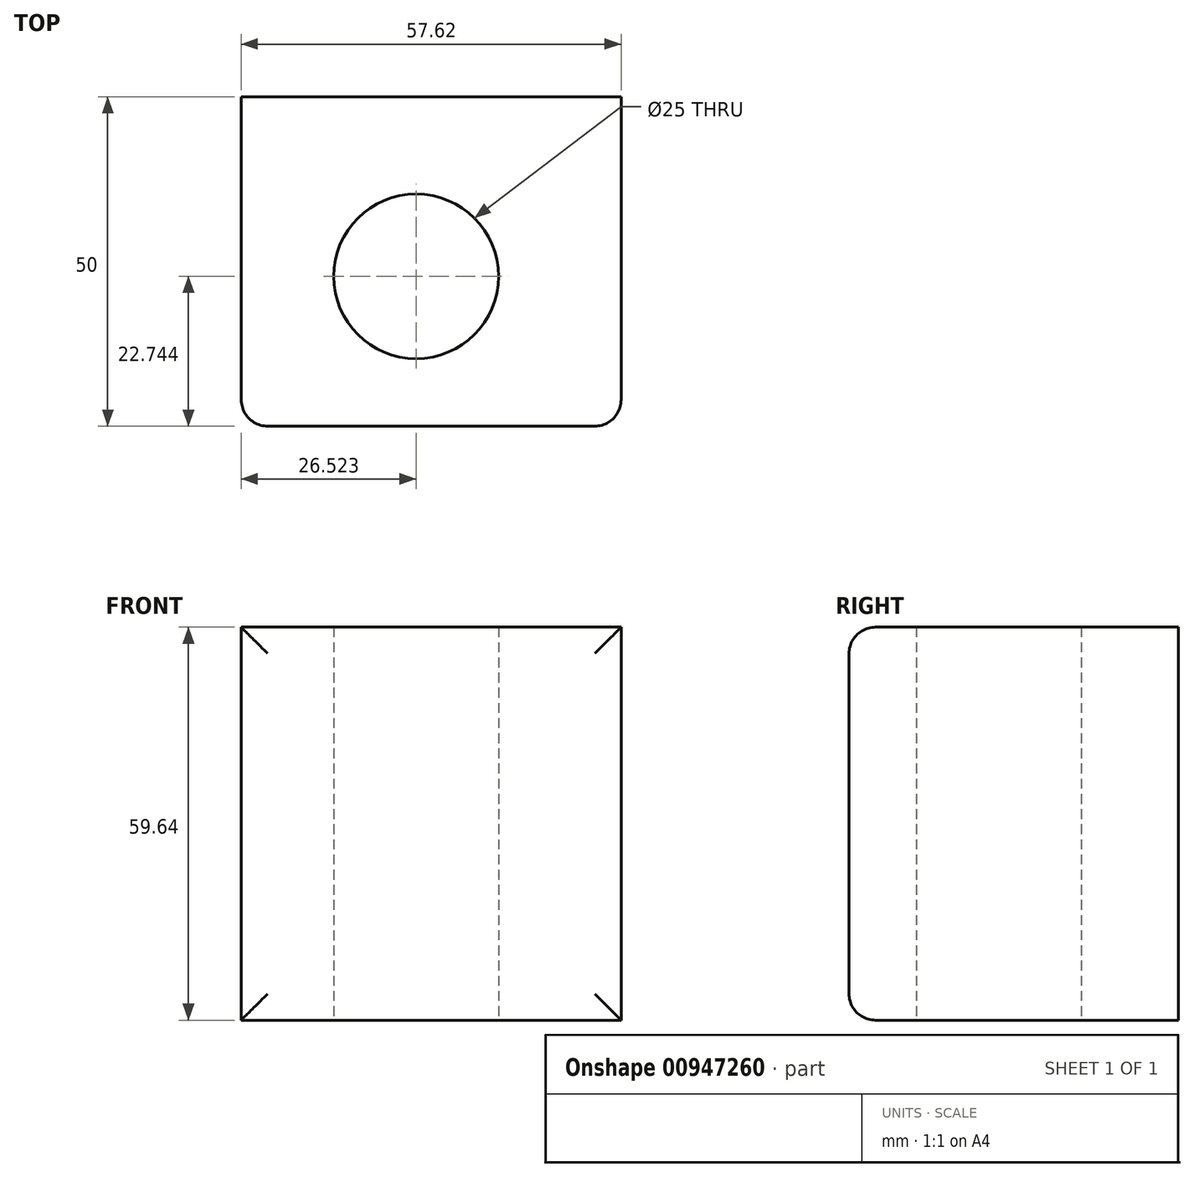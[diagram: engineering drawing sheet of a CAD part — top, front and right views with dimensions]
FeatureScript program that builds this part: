
annotation { "Feature Type Name" : "Feature", "Feature Type Description" : "" }
export const myFeature = defineFeature(function(context is Context, id is Id, definition is map)
    precondition{}
    {
        {
            var Q0;
            Q0=qCreatedBy(makeId("Front.planeOp"),FACE);
            var sketch = newSketch(context, id + "F0", { "sketchPlane" : qUnion([Q0])});
            skLineSegment(sketch, "E0.bottom", {"start": v(-28.81, 29.82) * mm, "end": v(28.81, 29.82) * mm});
            skLineSegment(sketch, "E0.top", {"start": v(-28.81, -29.82) * mm, "end": v(28.81, -29.82) * mm});
            skLineSegment(sketch, "E0.left", {"start": v(-28.81, 29.82) * mm, "end": v(-28.81, -29.82) * mm});
            skLineSegment(sketch, "E0.right", {"start": v(28.81, 29.82) * mm, "end": v(28.81, -29.82) * mm});
            skPoint(sketch, "E0.middle", {"position": v(0, 0) * mm});
            skSolve(sketch);
        }
        {
            var Q0;
            Q0=makeQuery(id+"F0.imprint","IMPRINT",FACE,{"disambiguationData":[TD([[makeQuery(id+"F0.imprint","IMPRINT",EDGE,{"derivedFrom":sQuery(id+"F0.wireOp",EDGE,"E0.bottom")}),-1.0]])]});
            extrude(context, id + "F1", {"entities" : qUnion([Q0]), "depth" : 50 * mm, "offsetDistance" : 25 * mm});
        }
        {
            var Q0;
            Q0=makeQuery(id+"F1.opExtrude","SWEPT_FACE",FACE,{"disambiguationData":[OSD([sQuery(id+"F0.wireOp",EDGE,"E0.top")])]});
            var sketch = newSketch(context, id + "F2", { "sketchPlane" : qUnion([Q0])});
            skCircle(sketch, "E1", {"center": v(-2.29, 27.26) * mm, "radius": 11.21 * mm});
            skSolve(sketch);
        }
        {
            var Q0;
            Q0=sQuery(id+"F2.wireOp",VERTEX,"E1.center");
            var Q1;
            Q1=makeQuery(id+"F1.opExtrude","SWEPT_BODY",BODY,{"disambiguationData":[OSD([sQuery(id+"F0.wireOp",EDGE,"E0.bottom"),sQuery(id+"F0.wireOp",EDGE,"E0.top"),sQuery(id+"F0.wireOp",EDGE,"E0.left"),sQuery(id+"F0.wireOp",EDGE,"E0.right")])]});
            hole(context, id + "F3", {"style" : HoleStyle.SIMPLE, "endStyle" : HoleEndStyle.THROUGH, "holeDiameter" : 25 * mm, "majorDiameter" : 5 * mm, "isTappedThrough" : true, "tappedDepth" : 12 * mm, "tapClearance" : 3, "locations" : qUnion([Q0]), "scope" : qUnion([Q1])});
        }
        {
            var Q0;
            Q0=makeQuery(id+"F1.opExtrude","CAP_EDGE",EDGE,{"disambiguationData":[OSD([sQuery(id+"F0.wireOp",EDGE,"E0.top")])],"isStart":false});
            var Q1;
            Q1=makeQuery(id+"F1.opExtrude","CAP_EDGE",EDGE,{"disambiguationData":[OSD([sQuery(id+"F0.wireOp",EDGE,"E0.left")])],"isStart":false});
            var Q2;
            Q2=makeQuery(id+"F1.opExtrude","CAP_EDGE",EDGE,{"disambiguationData":[OSD([sQuery(id+"F0.wireOp",EDGE,"E0.bottom")])],"isStart":false});
            var Q3;
            Q3=makeQuery(id+"F1.opExtrude","CAP_EDGE",EDGE,{"disambiguationData":[OSD([sQuery(id+"F0.wireOp",EDGE,"E0.right")])],"isStart":false});
            fillet(context, id + "F4", {"entities" : qUnion([Q0, Q1, Q2, Q3]), "radius" : 4 * mm, "tangentPropagation" : true, "allowEdgeOverflow" : false});
        }
    });
